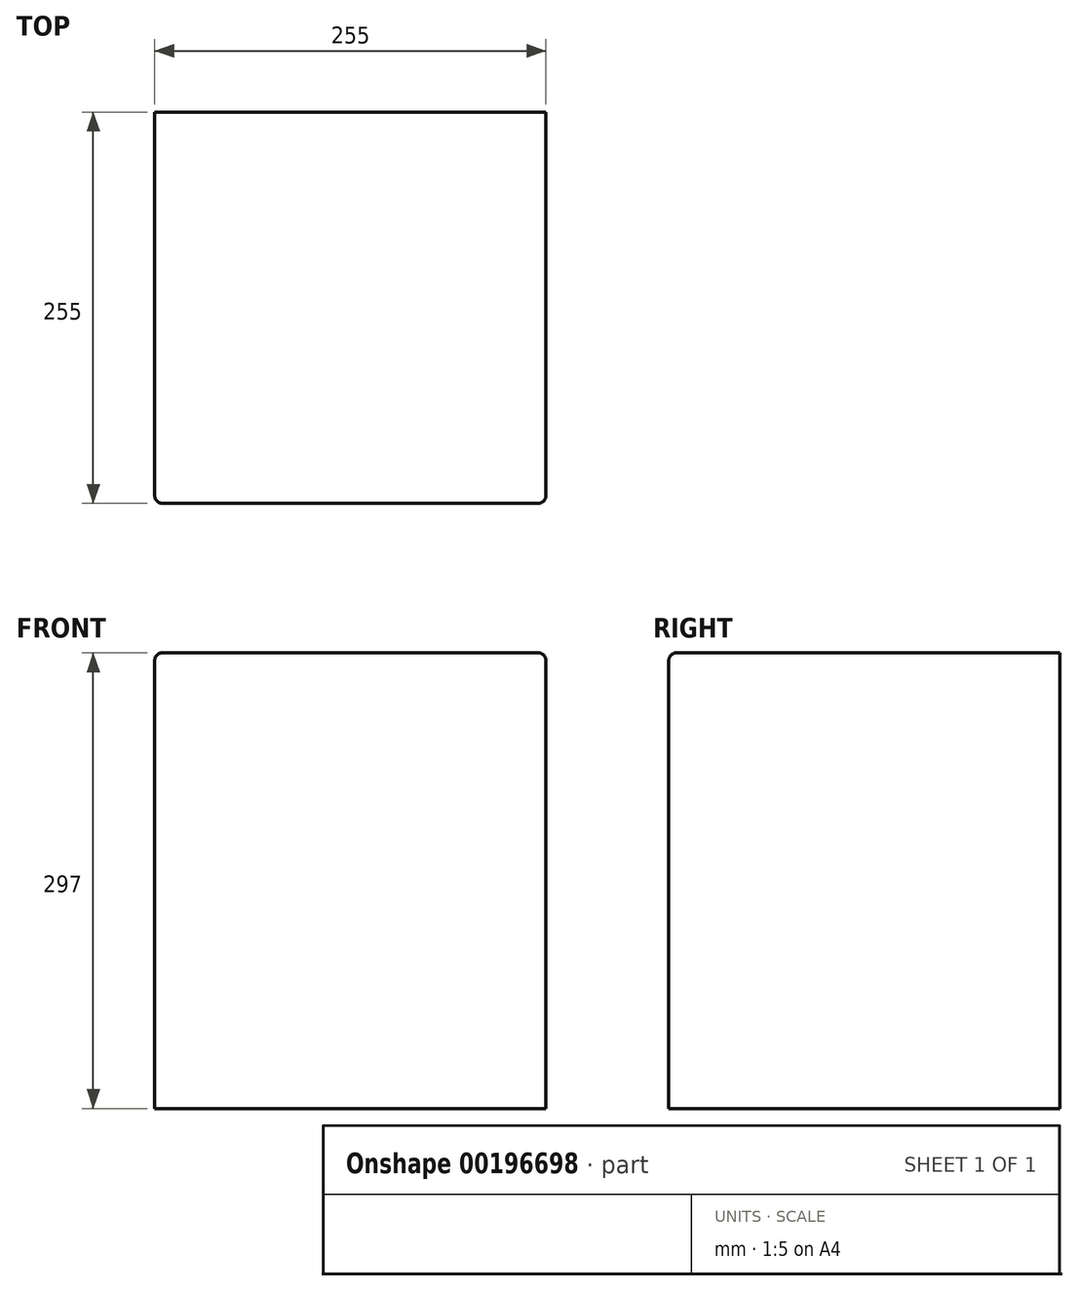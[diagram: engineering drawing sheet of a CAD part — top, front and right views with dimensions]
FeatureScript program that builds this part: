
annotation { "Feature Type Name" : "Feature", "Feature Type Description" : "" }
export const myFeature = defineFeature(function(context is Context, id is Id, definition is map)
    precondition{}
    {
        {
            var Q0;
            Q0=qCreatedBy(makeId("Top.planeOp"),FACE);
            var sketch = newSketch(context, id + "F0", { "sketchPlane" : qUnion([Q0])});
            skLineSegment(sketch, "E0.bottom", {"start": v(-202.84, 157.85) * mm, "end": v(52.16, 157.85) * mm});
            skLineSegment(sketch, "E0.top", {"start": v(-202.84, -97.15) * mm, "end": v(52.16, -97.15) * mm});
            skLineSegment(sketch, "E0.left", {"start": v(-202.84, 157.85) * mm, "end": v(-202.84, -97.15) * mm});
            skLineSegment(sketch, "E0.right", {"start": v(52.16, 157.85) * mm, "end": v(52.16, -97.15) * mm});
            skSolve(sketch);
        }
        {
            var Q0;
            Q0=makeQuery(id+"F0.imprint","IMPRINT",FACE,{"disambiguationData":[TD([[makeQuery(id+"F0.imprint","IMPRINT",EDGE,{"derivedFrom":sQuery(id+"F0.wireOp",EDGE,"E0.bottom")}),-1.0]])]});
            extrude(context, id + "F1", {"entities" : qUnion([Q0]), "depth" : 297 * mm});
        }
        {
            var Q0;
            Q0=makeQuery(id+"F1.opExtrude","CAP_EDGE",EDGE,{"disambiguationData":[OSD([sQuery(id+"F0.wireOp",EDGE,"E0.right")])],"isStart":false});
            var Q1;
            Q1=makeQuery(id+"F1.opExtrude","CAP_EDGE",EDGE,{"disambiguationData":[OSD([sQuery(id+"F0.wireOp",EDGE,"E0.left")])],"isStart":false});
            var Q2;
            Q2=makeQuery(id+"F1.opExtrude","SWEPT_EDGE",EDGE,{"disambiguationData":[OSD([sQuery(id+"F0.wireOp",EDGE,"E0.top"),sQuery(id+"F0.wireOp",EDGE,"E0.left")])]});
            var Q3;
            Q3=makeQuery(id+"F1.opExtrude","CAP_EDGE",EDGE,{"disambiguationData":[OSD([sQuery(id+"F0.wireOp",EDGE,"E0.top")])],"isStart":false});
            var Q4;
            Q4=makeQuery(id+"F1.opExtrude","SWEPT_EDGE",EDGE,{"disambiguationData":[OSD([sQuery(id+"F0.wireOp",EDGE,"E0.top"),sQuery(id+"F0.wireOp",EDGE,"E0.right")])]});
            fillet(context, id + "F2", {"entities" : qUnion([Q0, Q1, Q2, Q3, Q4]), "radius" : 5 * mm, "tangentPropagation" : true, "allowEdgeOverflow" : false});
        }
    });
